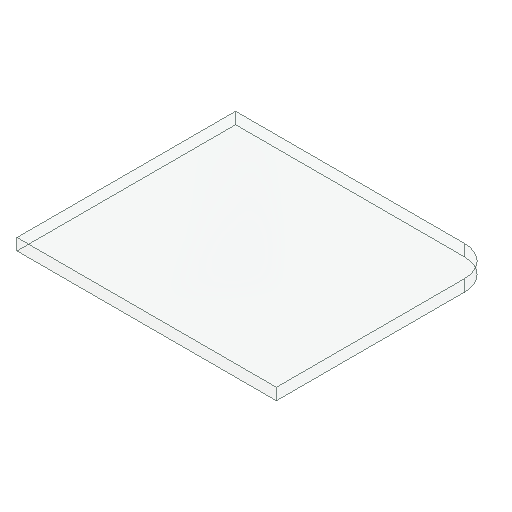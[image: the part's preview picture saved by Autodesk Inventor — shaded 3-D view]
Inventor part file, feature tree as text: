
AUTODESK INVENTOR PART (.ipt)
format: ipt  version: 2025 (Build 290162000, 162)  size: 120,320 bytes
history: native  units: mm
features: reference x5, extrude x2, sketch x2, other x2
ambient origin geometry x8: Origin, YZ Plane, XZ Plane, XY Plane, X Axis, Y Axis, Z Axis, Center Point
bodies: Solid1 (feature_tree)
feature tree (11):
  extrude  "Extrusion1"  Depth=40.0mm
  extrude  "Extrusion2"  Depth=10.0mm
  sketch  "Sketch1"  dims[d0=50.0mm d1=40.0mm]
  sketch  "Sketch2"  dims[d2=2.0mm d3=0.0mm d5=0.25mm d6=10.0mm d7=0.0mm d8=8.0mm]
  reference  "Reference1"
  reference  "Reference2"
  reference  "Reference3"
  reference  "Reference4"
  reference  "Reference5"
  other  "USB_C_PD_PPS_sink_with_enclosure.iam"
  other  "top_enclosure:1"
